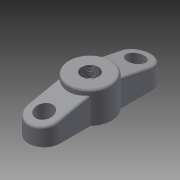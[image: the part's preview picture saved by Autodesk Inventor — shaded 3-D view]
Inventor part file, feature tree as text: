
AUTODESK INVENTOR PART (.ipt)
format: ipt  version: 2015 (Build 190159000, 159)  size: 173,056 bytes
history: native  units: in
note: dims shown in document units (in); Inventor stores cm internally (conversion verified against a paired STEP export)
features: extrude x3, fillet x3, sketch x3, thread x1
ambient origin geometry x8: Origin, YZ Plane, XZ Plane, XY Plane, X Axis, Y Axis, Z Axis, Center Point
bodies: Body1 (feature_tree)
feature tree (10):
  extrude  "Extrusion4"  Depth=2.7559in
  fillet  "Fillet1"  Radius=20.0787in
  extrude  "Extrusion6"  Depth=2.3622in
  extrude  "Extrusion7"  Depth=0.3937in TaperAngle=0.0deg
  thread  "Thread1"  [1 undecoded]
  fillet  "Fillet2"  Radius=2.5591in
  fillet  "Fillet3"  Radius=7.0866in
  sketch  "Sketch5"  dims[d9=20.0787in d10=2.7559in d11=20.0787in]
  sketch  "Sketch7"  dims[d12=4.3307in d13=2.3622in]
  sketch  "Sketch8"  dims[d14=2.3622in d17=5.1181in d18=0.0in d19=2.5591in d28=2.5591in d29=7.0866in d30=5.1181in d31=0.0in d32=2.7559in d33=5.1181in d34=0.0in d35=0.3937in d36=0.0in d37=0.3937in d38=0.3937in d39=2.7559in d40=2.7559in]
note: 1 required parameter value undecoded (feature->parameter linkage not recoverable at this tier; creation-order binding heuristic only, values carry confidence <= 0.55)
